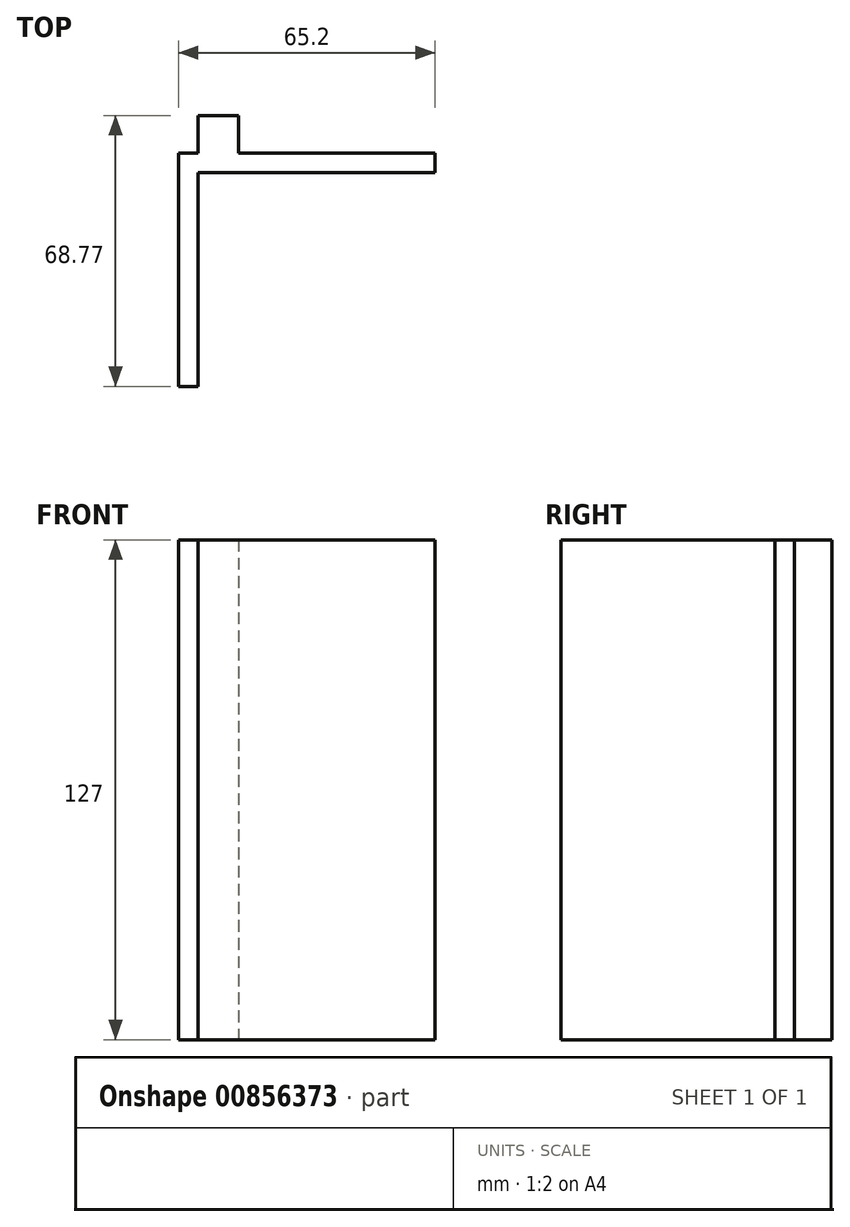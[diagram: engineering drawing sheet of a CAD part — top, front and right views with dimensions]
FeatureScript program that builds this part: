
annotation { "Feature Type Name" : "Feature", "Feature Type Description" : "" }
export const myFeature = defineFeature(function(context is Context, id is Id, definition is map)
    precondition{}
    {
        {
            var Q0;
            Q0=qCreatedBy(makeId("Top.planeOp"),FACE);
            var sketch = newSketch(context, id + "F0", { "sketchPlane" : qUnion([Q0])});
            skLineSegment(sketch, "E0.bottom", {"start": v(0, 0) * mm, "end": v(5, 0) * mm});
            skLineSegment(sketch, "E0.top", {"start": v(0, 43) * mm, "end": v(5, 43) * mm});
            skLineSegment(sketch, "E0.left", {"start": v(0, 0) * mm, "end": v(0, 43) * mm});
            skLineSegment(sketch, "E0.right", {"start": v(5, 0) * mm, "end": v(5, 43) * mm});
            skLineSegment(sketch, "E1.top", {"start": v(0, 59.27) * mm, "end": v(5, 59.27) * mm});
            skLineSegment(sketch, "E1.left", {"start": v(0, 43) * mm, "end": v(0, 59.27) * mm});
            skLineSegment(sketch, "E1.right", {"start": v(5, 43) * mm, "end": v(5, 59.27) * mm});
            skLineSegment(sketch, "E2.bottom", {"start": v(5, 59.27) * mm, "end": v(15.2, 59.27) * mm});
            skLineSegment(sketch, "E2.top", {"start": v(5, 54.27) * mm, "end": v(15.2, 54.27) * mm});
            skLineSegment(sketch, "E2.left", {"start": v(5, 59.27) * mm, "end": v(5, 54.27) * mm});
            skLineSegment(sketch, "E2.right", {"start": v(15.2, 59.27) * mm, "end": v(15.2, 54.27) * mm});
            skLineSegment(sketch, "E3.top", {"start": v(5, 68.77) * mm, "end": v(15.2, 68.77) * mm});
            skLineSegment(sketch, "E3.left", {"start": v(5, 59.27) * mm, "end": v(5, 68.77) * mm});
            skLineSegment(sketch, "E3.right", {"start": v(15.2, 59.27) * mm, "end": v(15.2, 68.77) * mm});
            skLineSegment(sketch, "E4.bottom", {"start": v(15.2, 59.27) * mm, "end": v(65.2, 59.27) * mm});
            skLineSegment(sketch, "E4.top", {"start": v(15.2, 54.27) * mm, "end": v(65.2, 54.27) * mm});
            skLineSegment(sketch, "E4.right", {"start": v(65.2, 59.27) * mm, "end": v(65.2, 54.27) * mm});
            skSolve(sketch);
        }
        {
            var Q0;
            Q0 = qSketchRegion(id + "F0", true);
            extrude(context, id + "F1", {"entities" : qUnion([Q0]), "depth" : 127 * mm, "offsetDistance" : 25.4 * mm});
        }
    });
